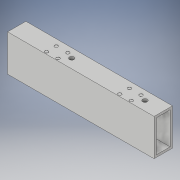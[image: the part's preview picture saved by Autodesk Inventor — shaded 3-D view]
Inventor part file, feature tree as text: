
AUTODESK INVENTOR PART (.ipt)
format: ipt  version: 2018 (Build 220112000, 112)  size: 129,536 bytes
history: native  units: in
note: dims shown in document units (in); Inventor stores cm internally (conversion verified against a paired STEP export)
features: extrude x3, sketch x3
ambient origin geometry x8: Origin, YZ Plane, XZ Plane, XY Plane, X Axis, Y Axis, Z Axis, Center Point
bodies: Solid1 (feature_tree)
feature tree (6):
  extrude  "Extrusion1"  Depth=1.0in
  extrude  "Extrusion2"  Depth=8.0in TaperAngle=0.0deg
  extrude  "Extrusion3"  Depth=0.01in TaperAngle=0.0deg
  sketch  "Sketch1"  dims[d0=2.0in d1=1.0in]
  sketch  "Sketch2"  dims[d2=0.125in d3=8.0in d4=0.0in]
  sketch  "Sketch3"  dims[d9=8.0in d10=0.0in d27=0.01in d28=0.0in d30=2.0in d31=0.25in d32=2.0in d33=0.25in]
